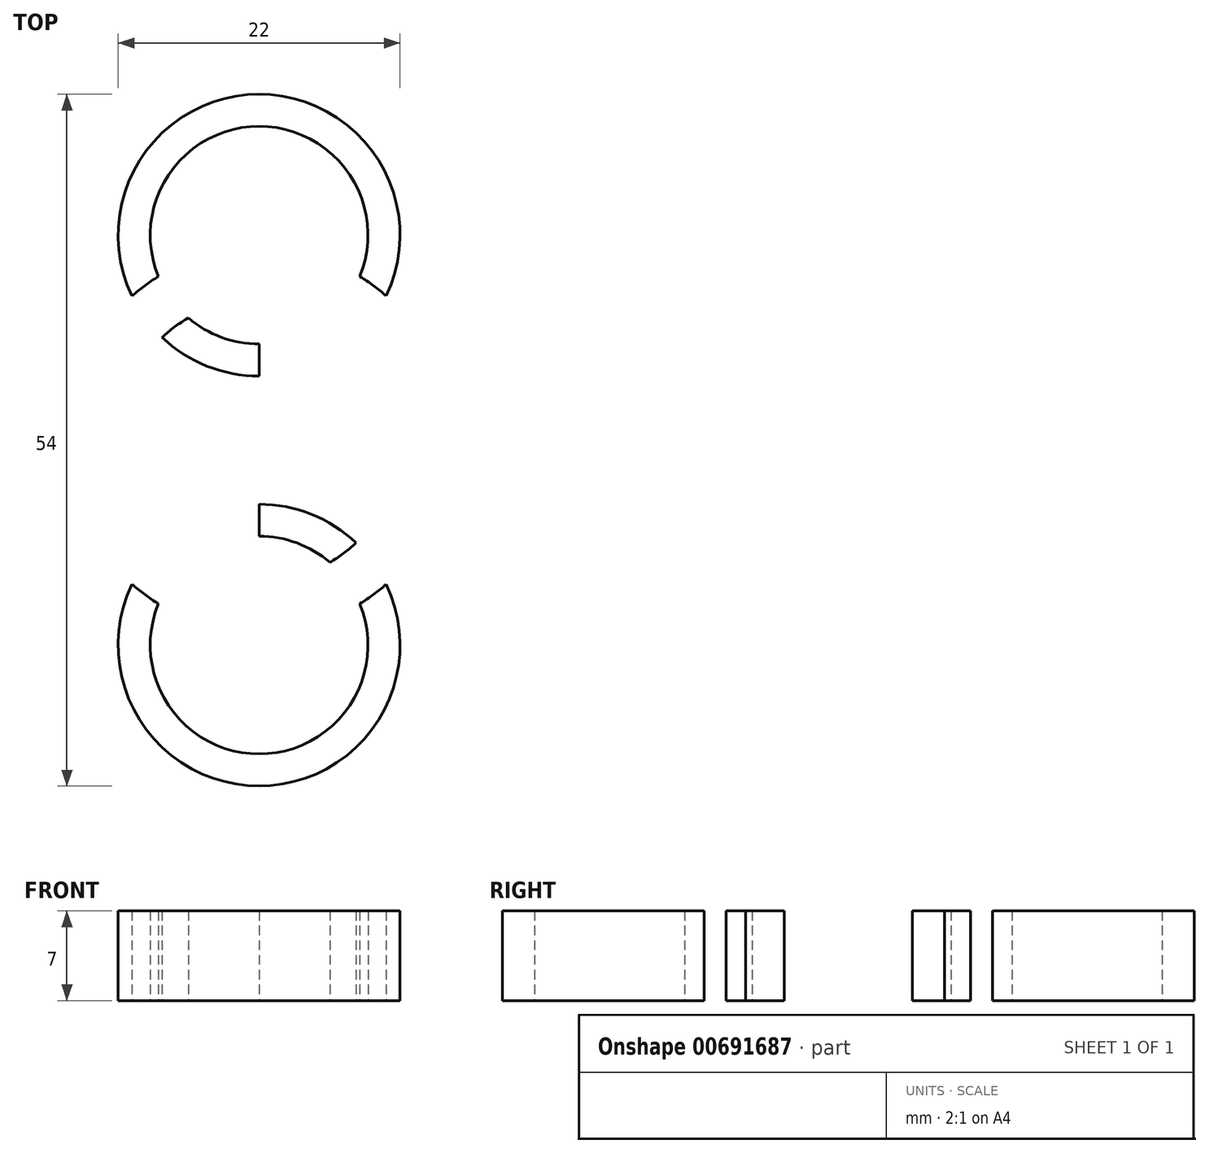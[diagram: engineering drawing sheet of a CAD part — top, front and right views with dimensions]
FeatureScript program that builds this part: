
annotation { "Feature Type Name" : "Feature", "Feature Type Description" : "" }
export const myFeature = defineFeature(function(context is Context, id is Id, definition is map)
    precondition{}
    {
        {
            var Q0;
            Q0=qCreatedBy(makeId("Top.planeOp"),FACE);
            var sketch = newSketch(context, id + "F0", { "sketchPlane" : qUnion([Q0])});
            skCircle(sketch, "E0", {"center": v(0, 0) * mm, "radius": 11.03 * mm});
            skCircle(sketch, "E1", {"center": v(0, 0) * mm, "radius": 15 * mm});
            skLineSegment(sketch, "E2", {"start": v(0, 0) * mm, "end": v(0, 32) * mm});
            skCircle(sketch, "E3", {"center": v(0, 16) * mm, "radius": 8.5 * mm});
            skCircle(sketch, "E4", {"center": v(0, 16) * mm, "radius": 11 * mm});
            skLineSegment(sketch, "E5.1.0", {"start": v(0, 0) * mm, "end": v(0, -32) * mm});
            skCircle(sketch, "E5.1.1", {"center": v(0, -16) * mm, "radius": 8.5 * mm});
            skCircle(sketch, "E5.1.3", {"center": v(0, -16) * mm, "radius": 11 * mm});
            skSolve(sketch);
        }
        {
            var Q0;
            {var subQ0=sQuery(id+"F0.wireOp",EDGE,"E1");var subQ1=sQuery(id+"F0.wireOp",EDGE,"E4");var subQ2=makeQuery(id+"F0.imprint","INTERSECT",VERTEX,{"disambiguationData":[OD(0.0)],"derivedFrom":[subQ1,subQ0]});Q0=makeQuery(id+"F0.imprint","IMPRINT",FACE,{"disambiguationData":[TD([[makeQuery(id+"F0.imprint","IMPRINT",EDGE,{"disambiguationData":[TD([[subQ2,-1.0]])],"derivedFrom":subQ1}),-1.0]])]});}
            var Q1;
            {var subQ0=sQuery(id+"F0.wireOp",EDGE,"E0");var subQ1=sQuery(id+"F0.wireOp",EDGE,"E5.1.1");var subQ2=makeQuery(id+"F0.imprint","INTERSECT",VERTEX,{"disambiguationData":[OD(1.0)],"derivedFrom":[subQ1,subQ0]});Q1=makeQuery(id+"F0.imprint","IMPRINT",FACE,{"disambiguationData":[TD([[makeQuery(id+"F0.imprint","IMPRINT",EDGE,{"disambiguationData":[TD([[subQ2,-1.0]])],"derivedFrom":subQ1}),-1.0]])]});}
            var Q2;
            {var subQ0=sQuery(id+"F0.wireOp",EDGE,"E5.1.3");var subQ1=sQuery(id+"F0.wireOp",EDGE,"E5.1.0");var subQ2=makeQuery(id+"F0.imprint","INTERSECT",VERTEX,{"disambiguationData":[OD(0.0)],"derivedFrom":[subQ1,subQ0]});Q2=makeQuery(id+"F0.imprint","IMPRINT",FACE,{"disambiguationData":[TD([[makeQuery(id+"F0.imprint","IMPRINT",EDGE,{"disambiguationData":[TD([[subQ2,1.0]])],"derivedFrom":subQ1}),-1.0]])]});}
            var Q3;
            {var subQ0=sQuery(id+"F0.wireOp",EDGE,"E5.1.3");var subQ1=sQuery(id+"F0.wireOp",EDGE,"E5.1.0");var subQ2=makeQuery(id+"F0.imprint","INTERSECT",VERTEX,{"disambiguationData":[OD(0.0)],"derivedFrom":[subQ1,subQ0]});Q3=makeQuery(id+"F0.imprint","IMPRINT",FACE,{"disambiguationData":[TD([[makeQuery(id+"F0.imprint","IMPRINT",EDGE,{"disambiguationData":[TD([[subQ2,1.0]])],"derivedFrom":subQ1}),1.0]])]});}
            var Q4;
            {var subQ0=sQuery(id+"F0.wireOp",EDGE,"E1");var subQ1=sQuery(id+"F0.wireOp",EDGE,"E5.1.1");var subQ2=makeQuery(id+"F0.imprint","INTERSECT",VERTEX,{"disambiguationData":[OD(0.0)],"derivedFrom":[subQ1,subQ0]});Q4=makeQuery(id+"F0.imprint","IMPRINT",FACE,{"disambiguationData":[TD([[makeQuery(id+"F0.imprint","IMPRINT",EDGE,{"disambiguationData":[TD([[subQ2,-1.0]])],"derivedFrom":subQ1}),-1.0]])]});}
            var Q5;
            {var subQ0=sQuery(id+"F0.wireOp",EDGE,"E1");var subQ1=sQuery(id+"F0.wireOp",EDGE,"E4");var subQ2=makeQuery(id+"F0.imprint","INTERSECT",VERTEX,{"disambiguationData":[OD(1.0)],"derivedFrom":[subQ1,subQ0]});Q5=makeQuery(id+"F0.imprint","IMPRINT",FACE,{"disambiguationData":[TD([[makeQuery(id+"F0.imprint","IMPRINT",EDGE,{"disambiguationData":[TD([[subQ2,1.0]])],"derivedFrom":subQ1}),-1.0]])]});}
            var Q6;
            {var subQ0=sQuery(id+"F0.wireOp",EDGE,"E0");var subQ1=sQuery(id+"F0.wireOp",EDGE,"E3");var subQ2=makeQuery(id+"F0.imprint","INTERSECT",VERTEX,{"disambiguationData":[OD(1.0)],"derivedFrom":[subQ1,subQ0]});Q6=makeQuery(id+"F0.imprint","IMPRINT",FACE,{"disambiguationData":[TD([[makeQuery(id+"F0.imprint","IMPRINT",EDGE,{"disambiguationData":[TD([[subQ2,-1.0]])],"derivedFrom":subQ1}),-1.0]])]});}
            var Q7;
            {var subQ0=sQuery(id+"F0.wireOp",EDGE,"E4");var subQ1=sQuery(id+"F0.wireOp",EDGE,"E2");var subQ2=makeQuery(id+"F0.imprint","INTERSECT",VERTEX,{"disambiguationData":[OD(0.0)],"derivedFrom":[subQ1,subQ0]});Q7=makeQuery(id+"F0.imprint","IMPRINT",FACE,{"disambiguationData":[TD([[makeQuery(id+"F0.imprint","IMPRINT",EDGE,{"disambiguationData":[TD([[subQ2,1.0]])],"derivedFrom":subQ1}),-1.0]])]});}
            var Q8;
            {var subQ0=sQuery(id+"F0.wireOp",EDGE,"E4");var subQ1=sQuery(id+"F0.wireOp",EDGE,"E2");var subQ2=makeQuery(id+"F0.imprint","INTERSECT",VERTEX,{"disambiguationData":[OD(0.0)],"derivedFrom":[subQ1,subQ0]});Q8=makeQuery(id+"F0.imprint","IMPRINT",FACE,{"disambiguationData":[TD([[makeQuery(id+"F0.imprint","IMPRINT",EDGE,{"disambiguationData":[TD([[subQ2,1.0]])],"derivedFrom":subQ1}),1.0]])]});}
            var Q9;
            {var subQ0=sQuery(id+"F0.wireOp",EDGE,"E1");var subQ1=sQuery(id+"F0.wireOp",EDGE,"E3");var subQ2=makeQuery(id+"F0.imprint","INTERSECT",VERTEX,{"disambiguationData":[OD(0.0)],"derivedFrom":[subQ1,subQ0]});Q9=makeQuery(id+"F0.imprint","IMPRINT",FACE,{"disambiguationData":[TD([[makeQuery(id+"F0.imprint","IMPRINT",EDGE,{"disambiguationData":[TD([[subQ2,-1.0]])],"derivedFrom":subQ1}),-1.0]])]});}
            extrude(context, id + "F1", {"entities" : qUnion([Q0, Q1, Q2, Q3, Q4, Q5, Q6, Q7, Q8, Q9]), "depth" : 7 * mm, "offsetDistance" : 25 * mm});
        }
    });
